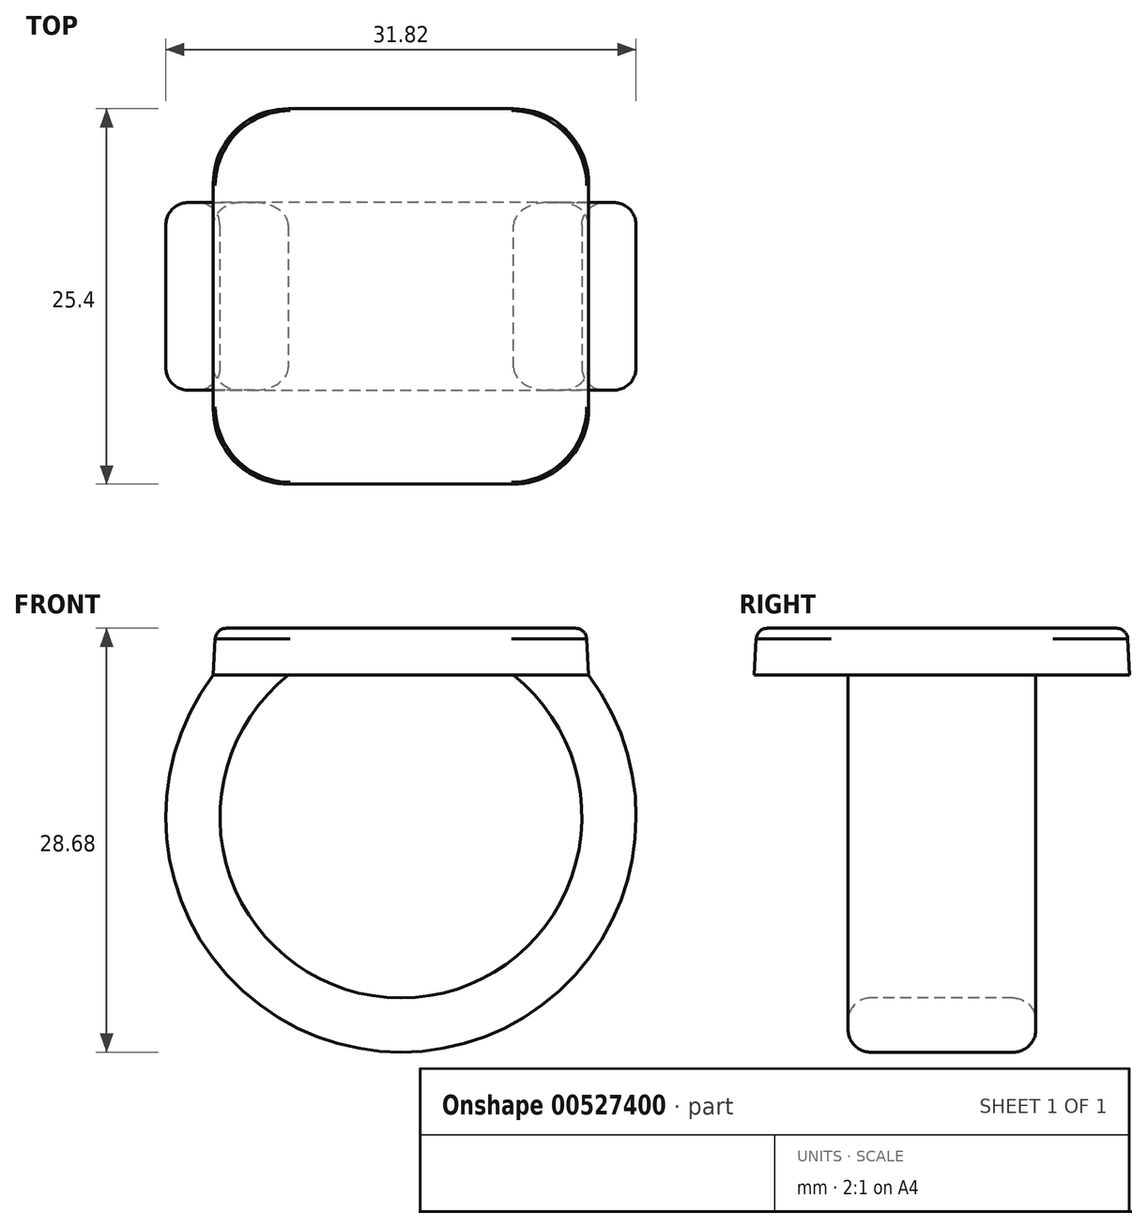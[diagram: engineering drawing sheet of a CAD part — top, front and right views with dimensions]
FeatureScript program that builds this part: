
annotation { "Feature Type Name" : "Feature", "Feature Type Description" : "" }
export const myFeature = defineFeature(function(context is Context, id is Id, definition is map)
    precondition{}
    {
        {
            var Q0;
            Q0=qCreatedBy(makeId("Top.planeOp"),FACE);
            var sketch = newSketch(context, id + "F0", { "sketchPlane" : qUnion([Q0])});
            skLineSegment(sketch, "E0.bottom", {"start": v(12.7, -12.7) * mm, "end": v(-12.7, -12.7) * mm});
            skLineSegment(sketch, "E0.top", {"start": v(12.7, 12.7) * mm, "end": v(-12.7, 12.7) * mm});
            skLineSegment(sketch, "E0.left", {"start": v(12.7, -12.7) * mm, "end": v(12.7, 12.7) * mm});
            skLineSegment(sketch, "E0.right", {"start": v(-12.7, -12.7) * mm, "end": v(-12.7, 12.7) * mm});
            skPoint(sketch, "E0.middle", {"position": v(0, 0) * mm});
            skSolve(sketch);
        }
        {
            var Q0;
            Q0 = qSketchRegion(id + "F0", true);
            extrude(context, id + "F1", {"entities" : qUnion([Q0]), "depth" : 3.17 * mm, "offsetDistance" : 25.4 * mm, "hasDraft" : true, "draftAngle" : 3 * degree, "draftPullDirection" : true});
        }
        {
            var Q0;
            Q0=qCreatedBy(makeId("Front.planeOp"),FACE);
            var sketch = newSketch(context, id + "F2", { "sketchPlane" : qUnion([Q0])});
            skArc(sketch, "E1", {"start": v(-10.16, 0) * mm, "mid": v(0, -23.56) * mm, "end": v(10.16, 0) * mm});
            skSolve(sketch);
        }
        {
            var Q0;
            Q0=makeQuery(id+"F1.opExtrude","CAP_FACE",FACE,{"disambiguationData":[OSD([sQuery(id+"F0.wireOp",EDGE,"E0.bottom"),sQuery(id+"F0.wireOp",EDGE,"E0.top"),sQuery(id+"F0.wireOp",EDGE,"E0.left"),sQuery(id+"F0.wireOp",EDGE,"E0.right")])],"isStart":true});
            var sketch = newSketch(context, id + "F3", { "sketchPlane" : qUnion([Q0])});
            skLineSegment(sketch, "E2.bottom", {"start": v(-7.62, -6.35) * mm, "end": v(-12.7, -6.35) * mm});
            skLineSegment(sketch, "E2.top", {"start": v(-7.62, 6.35) * mm, "end": v(-12.7, 6.35) * mm});
            skLineSegment(sketch, "E2.left", {"start": v(-7.62, -6.35) * mm, "end": v(-7.62, 6.35) * mm});
            skLineSegment(sketch, "E2.right", {"start": v(-12.7, -6.35) * mm, "end": v(-12.7, 6.35) * mm});
            skPoint(sketch, "E2.middle", {"position": v(-10.16, 0) * mm});
            skSolve(sketch);
        }
        {
            var Q0;
            Q0=makeQuery(id+"F3.imprint","IMPRINT",FACE,{"disambiguationData":[TD([[makeQuery(id+"F3.imprint","IMPRINT",EDGE,{"derivedFrom":sQuery(id+"F3.wireOp",EDGE,"E2.bottom")}),-1.0]])]});
            var Q1;
            Q1 = qConstructionFilter(qBodyType(qCreatedBy(id + "F2" ,EDGE), BodyType.WIRE), ConstructionObject.NO);
            sweep(context, id + "F4", {"operationType" : NewBodyOperationType.ADD, "profiles" : qUnion([Q0]), "path" : qUnion([Q1])});
        }
        {
            var Q0;
            Q0=qCreatedBy(makeId("Front.planeOp"),FACE);
            var sketch = newSketch(context, id + "F5", { "sketchPlane" : qUnion([Q0])});
            skLineSegment(sketch, "E3.0", {"start": v(10.16, 0) * mm, "end": v(7.62, 0) * mm});
            skLineSegment(sketch, "E3.1", {"start": v(10.01, -2.54) * mm, "end": v(10.16, 0) * mm});
            skArc(sketch, "E3.2", {"start": v(10.01, -2.54) * mm, "mid": v(8.9, -1.18) * mm, "end": v(7.62, 0) * mm});
            skPoint(sketch, "E4.trimOffspring.end.orphan", {"position": v(-12.7, 0) * mm});
            skPoint(sketch, "E5.orphan", {"position": v(-7.62, 0) * mm});
            skPoint(sketch, "E6.orphan", {"position": v(12.7, 0) * mm});
            skSolve(sketch);
        }
        {
            var Q0;
            Q0 = qSketchRegion(id + "F5", true);
            var Q1;
            Q1=makeQuery(id+"F4.opSweep","SWEPT_FACE",FACE,{"disambiguationData":[OSD([sQuery(id+"F2.wireOp",EDGE,"E1"),sQuery(id+"F3.wireOp",EDGE,"E2.top")])]});
            var Q2;
            Q2=makeQuery(id+"F4.opSweep","SWEPT_FACE",FACE,{"disambiguationData":[OSD([sQuery(id+"F2.wireOp",EDGE,"E1"),sQuery(id+"F3.wireOp",EDGE,"E2.bottom")])]});
            extrude(context, id + "F6", {"entities" : qUnion([Q0]), "operationType" : NewBodyOperationType.ADD, "endBound" : BoundingType.UP_TO_SURFACE, "depth" : 25.4 * mm, "endBoundEntityFace" : qUnion([Q1]), "offsetDistance" : 25.4 * mm, "hasSecondDirection" : true, "secondDirectionBound" : SecondDirectionBoundingType.UP_TO_SURFACE, "secondDirectionOppositeDirection" : true, "secondDirectionDepth" : 25.4 * mm, "secondDirectionBoundEntityFace" : qUnion([Q2])});
        }
        {
            var Q0;
            Q0=makeQuery(id+"F1.opExtrude","SWEPT_EDGE",EDGE,{"disambiguationData":[OSD([sQuery(id+"F0.wireOp",EDGE,"E0.top"),sQuery(id+"F0.wireOp",EDGE,"E0.left")])]});
            var Q1;
            Q1=makeQuery(id+"F1.opExtrude","SWEPT_EDGE",EDGE,{"disambiguationData":[OSD([sQuery(id+"F0.wireOp",EDGE,"E0.bottom"),sQuery(id+"F0.wireOp",EDGE,"E0.left")])]});
            var Q2;
            Q2=makeQuery(id+"F1.opExtrude","SWEPT_EDGE",EDGE,{"disambiguationData":[OSD([sQuery(id+"F0.wireOp",EDGE,"E0.bottom"),sQuery(id+"F0.wireOp",EDGE,"E0.right")])]});
            var Q3;
            Q3=makeQuery(id+"F1.opExtrude","SWEPT_EDGE",EDGE,{"disambiguationData":[OSD([sQuery(id+"F0.wireOp",EDGE,"E0.top"),sQuery(id+"F0.wireOp",EDGE,"E0.right")])]});
            fillet(context, id + "F7", {"entities" : qUnion([Q0, Q1, Q2, Q3]), "radius" : 5.08 * mm, "tangentPropagation" : true, "allowEdgeOverflow" : false});
        }
        {
            var Q0;
            Q0=makeQuery(id+"F4.opSweep","SWEPT_EDGE",EDGE,{"disambiguationData":[OSD([sQuery(id+"F0.wireOp",EDGE,"E0.right"),sQuery(id+"F2.wireOp",EDGE,"E1"),sQuery(id+"F3.wireOp",EDGE,"E2.bottom"),sQuery(id+"F3.wireOp",EDGE,"E2.right")])]});
            var Q1;
            {var subQ0=sQuery(id+"F3.wireOp",EDGE,"E2.bottom");var subQ1=sQuery(id+"F2.wireOp",EDGE,"E1");Q1=makeQuery(id+"F6.boolean.opBoolean","MERGE",EDGE,{"derivedFrom":[makeQuery(id+"F4.opSweep","SWEPT_EDGE",EDGE,{"disambiguationData":[OSD([subQ1,subQ0,sQuery(id+"F3.wireOp",EDGE,"E2.left")])]}),makeQuery(id+"F6.opExtrude","TWEAK_EDGE",EDGE,{"derivedFrom":[makeQuery(id+"F4.opSweep","SWEPT_FACE",FACE,{"disambiguationData":[OSD([subQ1,subQ0])]}),makeQuery(id+"F5.imprint","IMPRINT",EDGE,{"derivedFrom":sQuery(id+"F5.wireOp",EDGE,"E3.2")})]})]});}
            var Q2;
            Q2=makeQuery(id+"F4.opSweep","SWEPT_EDGE",EDGE,{"disambiguationData":[OSD([sQuery(id+"F0.wireOp",EDGE,"E0.right"),sQuery(id+"F2.wireOp",EDGE,"E1"),sQuery(id+"F3.wireOp",EDGE,"E2.top"),sQuery(id+"F3.wireOp",EDGE,"E2.right")])]});
            var Q3;
            {var subQ0=sQuery(id+"F3.wireOp",EDGE,"E2.top");var subQ1=sQuery(id+"F2.wireOp",EDGE,"E1");Q3=makeQuery(id+"F6.boolean.opBoolean","MERGE",EDGE,{"derivedFrom":[makeQuery(id+"F4.opSweep","SWEPT_EDGE",EDGE,{"disambiguationData":[OSD([subQ1,subQ0,sQuery(id+"F3.wireOp",EDGE,"E2.left")])]}),makeQuery(id+"F6.opExtrude","TWEAK_EDGE",EDGE,{"derivedFrom":[makeQuery(id+"F4.opSweep","SWEPT_FACE",FACE,{"disambiguationData":[OSD([subQ1,subQ0])]}),makeQuery(id+"F5.imprint","IMPRINT",EDGE,{"derivedFrom":sQuery(id+"F5.wireOp",EDGE,"E3.2")})]})]});}
            fillet(context, id + "F8", {"entities" : qUnion([Q0, Q1, Q2, Q3]), "radius" : 1.52 * mm, "tangentPropagation" : true, "allowEdgeOverflow" : false});
        }
        {
            var Q0;
            Q0=makeQuery(id+"F1.opExtrude","CAP_FACE",FACE,{"disambiguationData":[OSD([sQuery(id+"F0.wireOp",EDGE,"E0.bottom"),sQuery(id+"F0.wireOp",EDGE,"E0.top"),sQuery(id+"F0.wireOp",EDGE,"E0.left"),sQuery(id+"F0.wireOp",EDGE,"E0.right")])],"isStart":false});
            fillet(context, id + "F9", {"entities" : qUnion([Q0]), "radius" : 0.76 * mm, "tangentPropagation" : true, "allowEdgeOverflow" : false});
        }
    });
